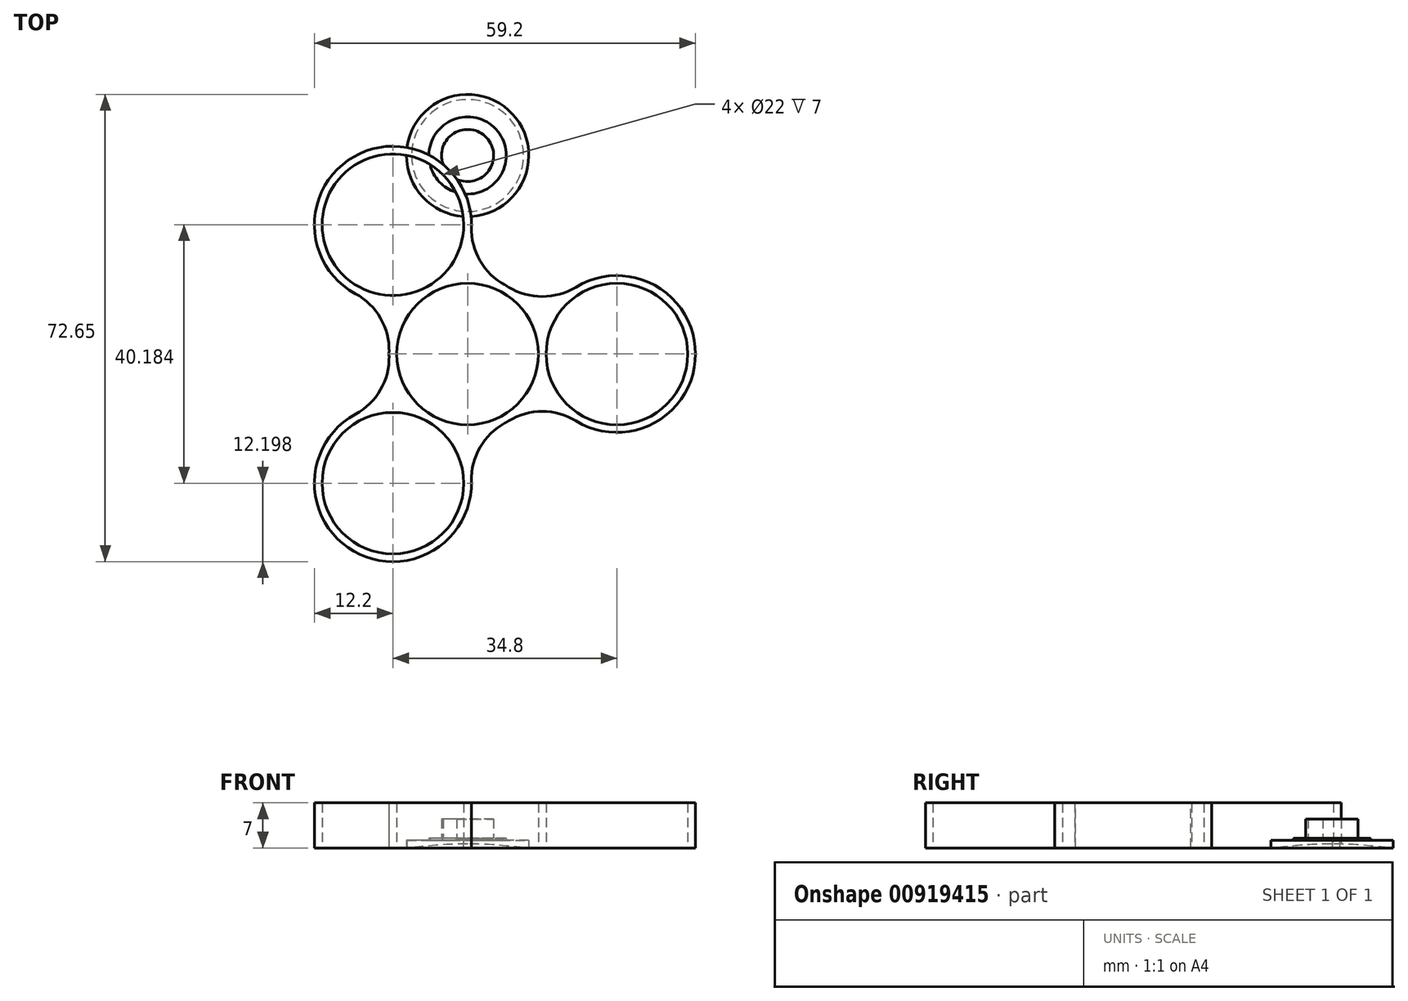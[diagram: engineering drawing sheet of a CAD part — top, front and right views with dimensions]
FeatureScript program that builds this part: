
annotation { "Feature Type Name" : "Feature", "Feature Type Description" : "" }
export const myFeature = defineFeature(function(context is Context, id is Id, definition is map)
    precondition{}
    {
        {
            var Q0;
            Q0=qCreatedBy(makeId("Top.planeOp"),FACE);
            var sketch = newSketch(context, id + "F0", { "sketchPlane" : qUnion([Q0])});
            skCircle(sketch, "E0", {"center": v(0, 0) * mm, "radius": 11 * mm});
            skCircle(sketch, "E1.0", {"center": v(0, 0) * mm, "radius": 12.2 * mm});
            skCircle(sketch, "E2", {"center": v(23.2, 0) * mm, "radius": 11 * mm});
            skCircle(sketch, "E3.0", {"center": v(23.2, 0) * mm, "radius": 12.2 * mm});
            skCircle(sketch, "E4.1.0", {"center": v(-11.6, 20.1) * mm, "radius": 12.2 * mm});
            skCircle(sketch, "E4.1.1", {"center": v(-11.6, 20.1) * mm, "radius": 11 * mm});
            skLineSegment(sketch, "E4.anchor1", {"start": v(0, 0) * mm, "end": v(23.2, 0) * mm, "construction": true});
            skLineSegment(sketch, "E4.anchor2", {"start": v(0, 0) * mm, "end": v(-11.6, -20.1) * mm, "construction": true});
            skCircle(sketch, "E5.1.2.0", {"center": v(-11.6, -20.1) * mm, "radius": 12.2 * mm});
            skCircle(sketch, "E5.2.2.0", {"center": v(-11.6, -20.1) * mm, "radius": 11 * mm});
            skSolve(sketch);
        }
        {
            var Q0;
            {var subQ3=sQuery(id+"F0.wireOp",EDGE,"E4.1.1");Q0=makeQuery(id+"F0.imprint","IMPRINT",FACE,{"disambiguationData":[TD([[makeQuery(id+"F0.imprint","IMPRINT",EDGE,{"derivedFrom":subQ3}),-1.0]])]});}
            var Q1;
            {var subQ0=sQuery(id+"F0.wireOp",EDGE,"E3.0");var subQ1=sQuery(id+"F0.wireOp",EDGE,"E0");var subQ2=makeQuery(id+"F0.imprint","INTERSECT",VERTEX,{"derivedFrom":[subQ1,subQ0]});Q1=makeQuery(id+"F0.imprint","IMPRINT",FACE,{"disambiguationData":[TD([[makeQuery(id+"F0.imprint","IMPRINT",EDGE,{"disambiguationData":[TD([[subQ2,-1.0]])],"derivedFrom":subQ1}),-1.0]])]});}
            var Q2;
            {var subQ0=sQuery(id+"F0.wireOp",EDGE,"E4.1.0");var subQ1=sQuery(id+"F0.wireOp",EDGE,"E1.0");var subQ2=makeQuery(id+"F0.imprint","INTERSECT",VERTEX,{"disambiguationData":[OD(0.0)],"derivedFrom":[subQ1,subQ0]});Q2=makeQuery(id+"F0.imprint","IMPRINT",FACE,{"disambiguationData":[TD([[makeQuery(id+"F0.imprint","IMPRINT",EDGE,{"disambiguationData":[TD([[subQ2,-1.0]])],"derivedFrom":subQ1}),1.0]])]});}
            var Q3;
            {var subQ0=sQuery(id+"F0.wireOp",EDGE,"E3.0");var subQ1=sQuery(id+"F0.wireOp",EDGE,"E0");var subQ2=makeQuery(id+"F0.imprint","INTERSECT",VERTEX,{"derivedFrom":[subQ1,subQ0]});Q3=makeQuery(id+"F0.imprint","IMPRINT",FACE,{"disambiguationData":[TD([[makeQuery(id+"F0.imprint","IMPRINT",EDGE,{"disambiguationData":[TD([[subQ2,1.0]])],"derivedFrom":subQ1}),-1.0]])]});}
            var Q4;
            {var subQ0=sQuery(id+"F0.wireOp",EDGE,"E3.0");var subQ1=sQuery(id+"F0.wireOp",EDGE,"E1.0");var subQ2=makeQuery(id+"F0.imprint","INTERSECT",VERTEX,{"disambiguationData":[OD(0.0)],"derivedFrom":[subQ1,subQ0]});Q4=makeQuery(id+"F0.imprint","IMPRINT",FACE,{"disambiguationData":[TD([[makeQuery(id+"F0.imprint","IMPRINT",EDGE,{"disambiguationData":[TD([[subQ2,1.0]])],"derivedFrom":subQ1}),1.0]])]});}
            var Q5;
            {var subQ3=sQuery(id+"F0.wireOp",EDGE,"E2");Q5=makeQuery(id+"F0.imprint","IMPRINT",FACE,{"disambiguationData":[TD([[makeQuery(id+"F0.imprint","IMPRINT",EDGE,{"derivedFrom":subQ3}),-1.0]])]});}
            var Q6;
            {var subQ0=sQuery(id+"F0.wireOp",EDGE,"E4.1.0");var subQ1=sQuery(id+"F0.wireOp",EDGE,"E0");var subQ2=makeQuery(id+"F0.imprint","INTERSECT",VERTEX,{"derivedFrom":[subQ1,subQ0]});Q6=makeQuery(id+"F0.imprint","IMPRINT",FACE,{"disambiguationData":[TD([[makeQuery(id+"F0.imprint","IMPRINT",EDGE,{"disambiguationData":[TD([[subQ2,-1.0]])],"derivedFrom":subQ1}),-1.0]])]});}
            var Q7;
            {var subQ0=sQuery(id+"F0.wireOp",EDGE,"E5.1.2.0");var subQ1=sQuery(id+"F0.wireOp",EDGE,"E1.0");var subQ2=makeQuery(id+"F0.imprint","INTERSECT",VERTEX,{"disambiguationData":[OD(0.0)],"derivedFrom":[subQ1,subQ0]});Q7=makeQuery(id+"F0.imprint","IMPRINT",FACE,{"disambiguationData":[TD([[makeQuery(id+"F0.imprint","IMPRINT",EDGE,{"disambiguationData":[TD([[subQ2,-1.0]])],"derivedFrom":subQ1}),1.0]])]});}
            var Q8;
            {var subQ3=sQuery(id+"F0.wireOp",EDGE,"E5.2.2.0");Q8=makeQuery(id+"F0.imprint","IMPRINT",FACE,{"disambiguationData":[TD([[makeQuery(id+"F0.imprint","IMPRINT",EDGE,{"derivedFrom":subQ3}),-1.0]])]});}
            extrude(context, id + "F1", {"entities" : qUnion([Q0, Q1, Q2, Q3, Q4, Q5, Q6, Q7, Q8]), "depth" : 7 * mm, "offsetDistance" : 25 * mm});
        }
        {
            var Q0;
            {var subQ0=sQuery(id+"F0.wireOp",EDGE,"E4.1.0");var subQ1=sQuery(id+"F0.wireOp",EDGE,"E1.0");Q0=makeQuery(id+"F1.opExtrude","SWEPT_EDGE",EDGE,{"disambiguationData":[OSD([subQ1,subQ0]),TDD([makeQuery(id+"F0.imprint","INTERSECT",VERTEX,{"disambiguationData":[OD(1.0)],"derivedFrom":[subQ1,subQ0]})])]});}
            var Q1;
            {var subQ0=sQuery(id+"F0.wireOp",EDGE,"E3.0");var subQ1=sQuery(id+"F0.wireOp",EDGE,"E1.0");Q1=makeQuery(id+"F1.opExtrude","SWEPT_EDGE",EDGE,{"disambiguationData":[OSD([subQ1,subQ0]),TDD([makeQuery(id+"F0.imprint","INTERSECT",VERTEX,{"disambiguationData":[OD(1.0)],"derivedFrom":[subQ1,subQ0]})])]});}
            var Q2;
            {var subQ0=sQuery(id+"F0.wireOp",EDGE,"E3.0");var subQ1=sQuery(id+"F0.wireOp",EDGE,"E1.0");Q2=makeQuery(id+"F1.opExtrude","SWEPT_EDGE",EDGE,{"disambiguationData":[OSD([subQ1,subQ0]),TDD([makeQuery(id+"F0.imprint","INTERSECT",VERTEX,{"disambiguationData":[OD(0.0)],"derivedFrom":[subQ1,subQ0]})])]});}
            var Q3;
            {var subQ0=sQuery(id+"F0.wireOp",EDGE,"E4.1.0");var subQ1=sQuery(id+"F0.wireOp",EDGE,"E1.0");Q3=makeQuery(id+"F1.opExtrude","SWEPT_EDGE",EDGE,{"disambiguationData":[OSD([subQ1,subQ0]),TDD([makeQuery(id+"F0.imprint","INTERSECT",VERTEX,{"disambiguationData":[OD(0.0)],"derivedFrom":[subQ1,subQ0]})])]});}
            var Q4;
            {var subQ0=sQuery(id+"F0.wireOp",EDGE,"E5.1.2.0");var subQ1=sQuery(id+"F0.wireOp",EDGE,"E1.0");Q4=makeQuery(id+"F1.opExtrude","SWEPT_EDGE",EDGE,{"disambiguationData":[OSD([subQ1,subQ0]),TDD([makeQuery(id+"F0.imprint","INTERSECT",VERTEX,{"disambiguationData":[OD(1.0)],"derivedFrom":[subQ1,subQ0]})])]});}
            var Q5;
            {var subQ0=sQuery(id+"F0.wireOp",EDGE,"E5.1.2.0");var subQ1=sQuery(id+"F0.wireOp",EDGE,"E1.0");Q5=makeQuery(id+"F1.opExtrude","SWEPT_EDGE",EDGE,{"disambiguationData":[OSD([subQ1,subQ0]),TDD([makeQuery(id+"F0.imprint","INTERSECT",VERTEX,{"disambiguationData":[OD(0.0)],"derivedFrom":[subQ1,subQ0]})])]});}
            fillet(context, id + "F2", {"entities" : qUnion([Q0, Q1, Q2, Q3, Q4, Q5]), "radius" : 10 * mm, "tangentPropagation" : true, "allowEdgeOverflow" : false});
        }
        {
            var Q0;
            Q0=qCreatedBy(makeId("Top.planeOp"),FACE);
            var sketch = newSketch(context, id + "F3", { "sketchPlane" : qUnion([Q0])});
            skCircle(sketch, "E6", {"center": v(0, 30.86) * mm, "radius": 9.5 * mm});
            skSolve(sketch);
        }
        {
            var Q0;
            Q0=qSketchRegion(id+"F3",true);
            extrude(context, id + "F4", {"entities" : qUnion([Q0]), "depth" : 1.2 * mm, "offsetDistance" : 25 * mm});
        }
        {
            var Q0;
            Q0=makeQuery(id+"F4.opExtrude","CAP_FACE",FACE,{"disambiguationData":[OSD([sQuery(id+"F3.wireOp",EDGE,"E6")])],"isStart":false});
            var sketch = newSketch(context, id + "F5", { "sketchPlane" : qUnion([Q0])});
            skCircle(sketch, "E7", {"center": v(0, 30.86) * mm, "radius": 6 * mm});
            skSolve(sketch);
        }
        {
            var Q0;
            Q0=qSketchRegion(id+"F5",true);
            extrude(context, id + "F6", {"entities" : qUnion([Q0]), "operationType" : NewBodyOperationType.ADD, "depth" : .3 * mm, "offsetDistance" : 25 * mm});
        }
        {
            var Q0;
            Q0=makeQuery(id+"F6.opExtrude","CAP_FACE",FACE,{"disambiguationData":[OSD([sQuery(id+"F5.wireOp",EDGE,"E7")])],"isStart":false});
            var sketch = newSketch(context, id + "F7", { "sketchPlane" : qUnion([Q0])});
            skCircle(sketch, "E8", {"center": v(0, 30.86) * mm, "radius": 4.05 * mm});
            skSolve(sketch);
        }
        {
            var Q0;
            Q0=qSketchRegion(id+"F7",true);
            extrude(context, id + "F8", {"entities" : qUnion([Q0]), "operationType" : NewBodyOperationType.ADD, "depth" : 3 * mm, "offsetDistance" : 25 * mm});
        }
        {
            var Q0;
            Q0=qCreatedBy(makeId("Right.planeOp"),FACE);
            var sketch = newSketch(context, id + "F9", { "sketchPlane" : qUnion([Q0])});
            skLineSegment(sketch, "E9.0", {"start": v(21.36, 0) * mm, "end": v(40.36, 0) * mm});
            skLineSegment(sketch, "E10.0", {"start": v(21.36, 1.2) * mm, "end": v(40.36, 1.2) * mm});
            skArc(sketch, "E11", {"start": v(39.56, 0) * mm, "mid": v(30.86, 0.6) * mm, "end": v(22.16, 0) * mm});
            skLineSegment(sketch, "E12", {"start": v(30.86, 0.6) * mm, "end": v(30.86, 0) * mm});
            skSolve(sketch);
        }
        {
            var Q0;
            {var subQ3=sQuery(id+"F9.wireOp",EDGE,"E12");Q0=makeQuery(id+"F9.imprint","IMPRINT",FACE,{"disambiguationData":[TD([[makeQuery(id+"F9.imprint","IMPRINT",EDGE,{"derivedFrom":subQ3}),-1.0]])]});}
            var Q1;
            Q1=sQuery(id+"F9.wireOp",EDGE,"E12");
            revolve(context, id + "F10", {"operationType" : NewBodyOperationType.REMOVE, "surfaceOperationType" : NewSurfaceOperationType.NEW, "entities" : qUnion([Q0]), "axis" : qUnion([Q1]), "revolveType" : RevolveType.FULL, "oppositeDirection" : true});
        }
    });
